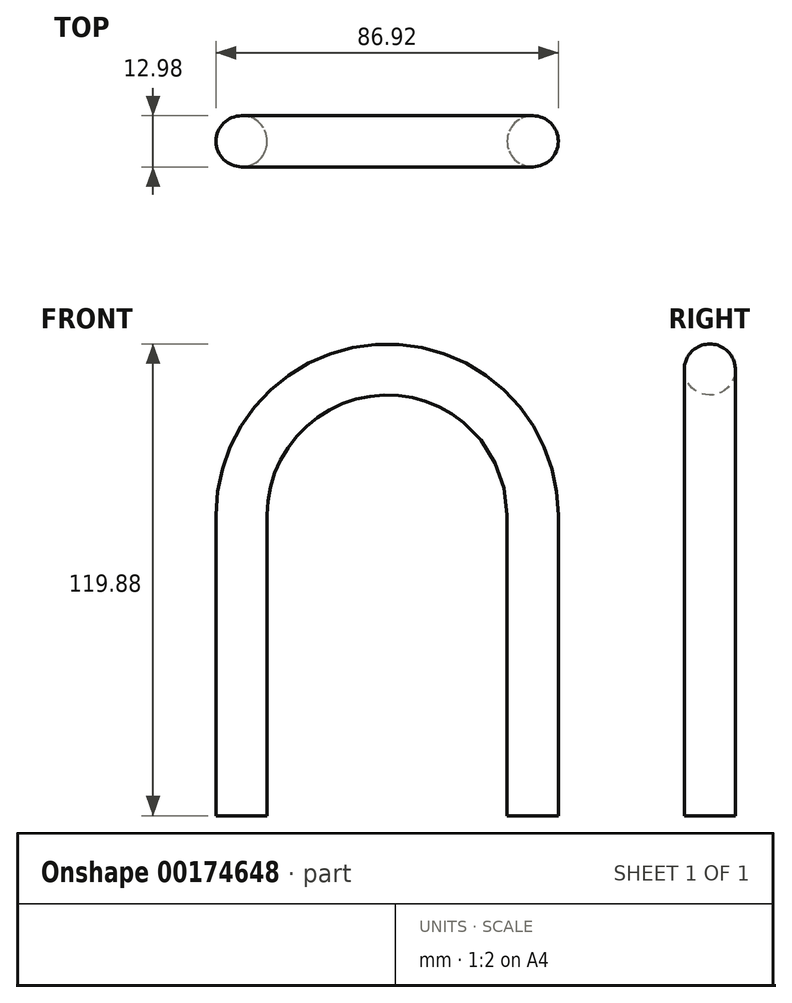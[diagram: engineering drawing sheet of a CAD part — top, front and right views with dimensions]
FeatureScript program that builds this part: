
annotation { "Feature Type Name" : "Feature", "Feature Type Description" : "" }
export const myFeature = defineFeature(function(context is Context, id is Id, definition is map)
    precondition{}
    {
        {
            var Q0;
            Q0=qCreatedBy(makeId("Front.planeOp"),FACE);
            var sketch = newSketch(context, id + "F0", { "sketchPlane" : qUnion([Q0])});
            skLineSegment(sketch, "E0", {"start": v(37.38, -26.3) * mm, "end": v(37.38, 50.11) * mm});
            skLineSegment(sketch, "E1", {"start": v(37.38, 50.11) * mm, "end": v(37.38, 50.11) * mm});
            skLineSegment(sketch, "E2", {"start": v(-36.76, 50.11) * mm, "end": v(-36.76, -26.3) * mm});
            skArc(sketch, "E3", {"start": v(37.38, 50.11) * mm, "mid": v(0.3, 87.18) * mm, "end": v(-36.76, 50.11) * mm});
            skLineSegment(sketch, "E4.trimOffspring", {"start": v(-36.76, 50.11) * mm, "end": v(-36.76, 50.11) * mm});
            skSolve(sketch);
        }
        {
            var Q0;
            Q0=qCreatedBy(makeId("Top.planeOp"),FACE);
            var sketch = newSketch(context, id + "F1", { "sketchPlane" : qUnion([Q0])});
            skCircle(sketch, "E5", {"center": v(37.28, 0) * mm, "radius": 6.5 * mm});
            skSolve(sketch);
        }
        {
            var Q0;
            Q0=makeQuery(id+"F1.imprint","IMPRINT",FACE,{"disambiguationData":[TD([[makeQuery(id+"F1.imprint","IMPRINT",EDGE,{"derivedFrom":sQuery(id+"F1.wireOp",EDGE,"E5")}),1.0]])]});
            var Q1;
            Q1=sQuery(id+"F0.wireOp",EDGE,"E0");
            var Q2;
            Q2=sQuery(id+"F0.wireOp",EDGE,"E2");
            var Q3;
            Q3=sQuery(id+"F0.wireOp",EDGE,"E3");
            sweep(context, id + "F2", {"profiles" : qUnion([Q0]), "path" : qUnion([Q1, Q2, Q3])});
        }
    });
